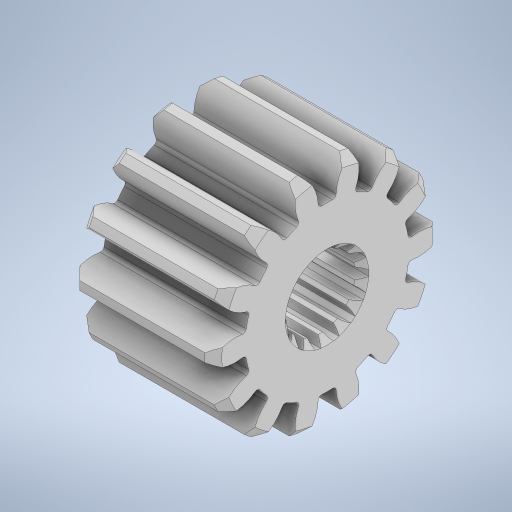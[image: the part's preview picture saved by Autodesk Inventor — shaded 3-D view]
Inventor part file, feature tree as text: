
AUTODESK INVENTOR PART (.ipt)
format: ipt  version: 2023 (Build 270158030, 158C)  size: 588,288 bytes
history: native  units: in
note: dims shown in document units (in); Inventor stores cm internally (conversion verified against a paired STEP export)
features: sketch x1, pattern_circular x1
ambient origin geometry x8: Origin, YZ Plane, XZ Plane, XY Plane, X Axis, Y Axis, Z Axis, Center Point
bodies: Solid1 (feature_tree)
feature tree (2):
  sketch  "Sketch1"  dims[d0=0.7in]
  pattern_circular  "CirPattern1"
